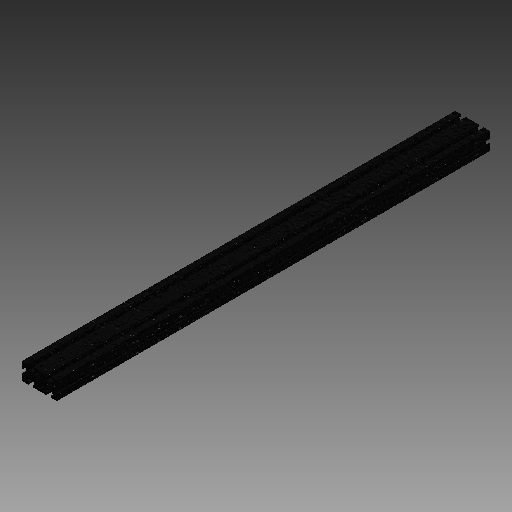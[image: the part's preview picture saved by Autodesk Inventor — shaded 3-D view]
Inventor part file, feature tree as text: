
AUTODESK INVENTOR PART (.ipt)
format: ipt  version: 2019 (Build 230136000, 136)  size: 345,088 bytes
history: native  units: in
note: dims shown in document units (in); Inventor stores cm internally (conversion verified against a paired STEP export)
features: extrude x1, sketch x1
ambient origin geometry x8: Origin, YZ Plane, XZ Plane, XY Plane, X Axis, Y Axis, Z Axis, Center Point
bodies: Solid1 (feature_tree)
feature tree (2):
  extrude  "Extrusion1"  [1 undecoded]
  sketch  "Sketch1"  dims[d0=36.0in d1=0.0in]
note: 1 required parameter value undecoded (feature->parameter linkage not recoverable at this tier; creation-order binding heuristic only, values carry confidence <= 0.55)
